# Revit family: FU_Inspec_Grade_Plus_2-10
name_source: partatom
category: Furniture
units: mm (PartAtom-declared; Revit-internal decimal feet)

## family parameters
Always vertical = Yes
Cut with Voids When Loaded = No
OmniClass Number = 23.40.20.00
OmniClass Title = General Furniture and Specialties
Room Calculation Point = No
Shared = No
Work Plane-Based = No

## types (2) — shared parameters
Assembly Code = E2020
Depth = 670 mm
Frame Material = Metal - Chrome - Polished
Height = 880 mm
Keynote = 46.B
Manufacturer = Inspec
Seat Pad Material = Colour - Khaki
URL = https://inspecfurniture.com
Weight = 8.1 kg
Width = 700 mm
zero-valued in all types: Default Elevation

## per-type parameters (varying)
| type | Description | Model | Seat Material |
| Grade Plus 2.9 - Chrome - White | 360° swivel armchair with recycled polypropylene seat on a polished aluminum 4 foot base. With adjustable height and casters | Grade Plus 2.9 | Plastic - White |
| Grade Plus 2.10 - Chrome - Red | 360° swivel armchair with recycled polypropylene seat on a polished aluminum 4 foot base. With upholstered seat pad, adjustable height and casters | Grade Plus 2.10 | Plastic - Red |

## geometry (parser evidence)
native form markers: Sweep x2
no freeform markers — native parametric forms only
